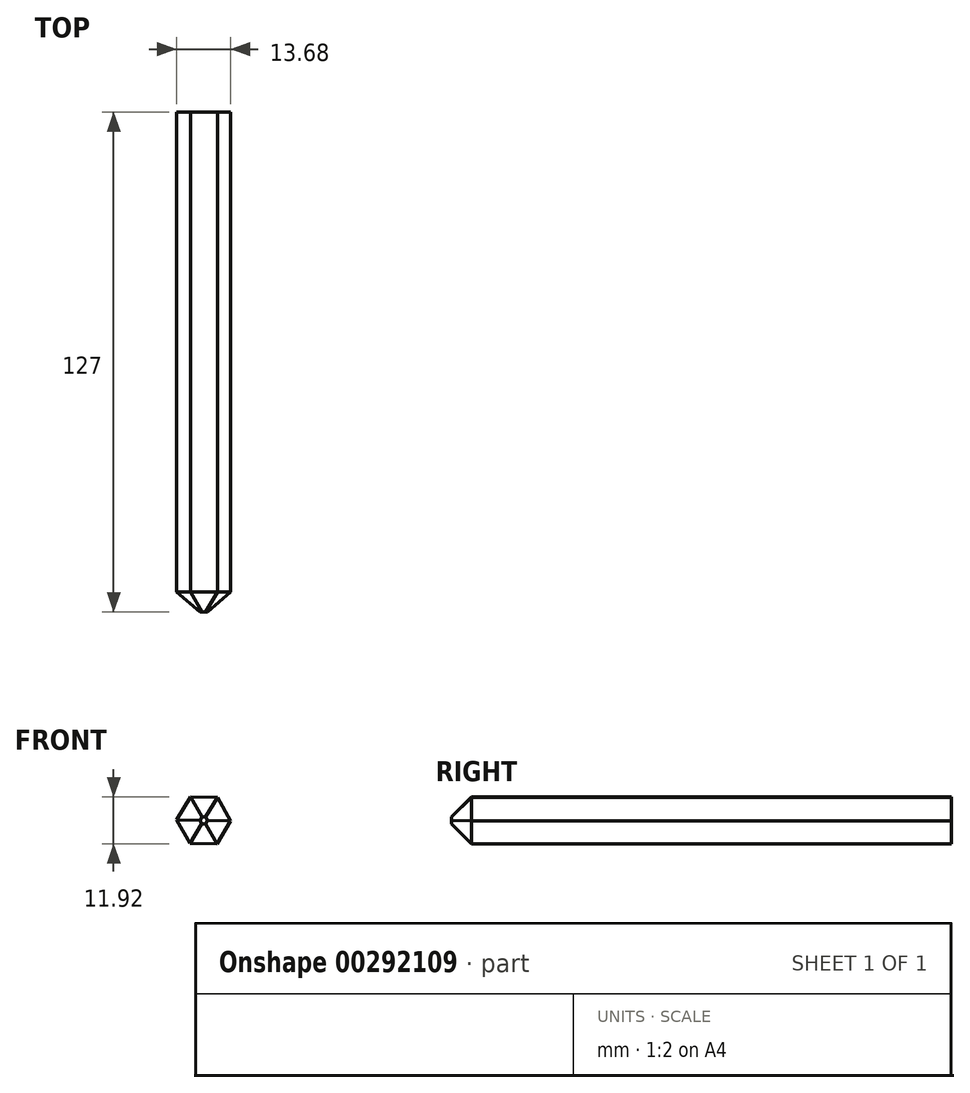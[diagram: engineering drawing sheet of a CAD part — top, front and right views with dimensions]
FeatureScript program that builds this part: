
annotation { "Feature Type Name" : "Feature", "Feature Type Description" : "" }
export const myFeature = defineFeature(function(context is Context, id is Id, definition is map)
    precondition{}
    {
        {
            var Q0;
            Q0=qCreatedBy(makeId("Front.planeOp"),FACE);
            var sketch = newSketch(context, id + "F0", { "sketchPlane" : qUnion([Q0])});
            skCircle(sketch, "E0", {"center": v(0, 0) * mm, "radius": 6.97 * mm});
            skSolve(sketch);
        }
        {
            var Q0;
            Q0=qCreatedBy(makeId("Front.planeOp"),FACE);
            var sketch = newSketch(context, id + "F1", { "sketchPlane" : qUnion([Q0])});
            skCircle(sketch, "E1.cCircle", {"center": v(0, 0) * mm, "radius": 5.92 * mm, "construction": true});
            skLineSegment(sketch, "E1.0", {"start": v(3.49, 5.88) * mm, "end": v(6.84, -0.08) * mm});
            skLineSegment(sketch, "E1.1", {"start": v(6.84, -0.08) * mm, "end": v(3.35, -5.96) * mm});
            skLineSegment(sketch, "E1.2", {"start": v(3.35, -5.96) * mm, "end": v(-3.49, -5.88) * mm});
            skLineSegment(sketch, "E1.3", {"start": v(-3.49, -5.88) * mm, "end": v(-6.84, 0.08) * mm});
            skLineSegment(sketch, "E1.4", {"start": v(-6.84, 0.08) * mm, "end": v(-3.35, 5.96) * mm});
            skLineSegment(sketch, "E1.5", {"start": v(-3.35, 5.96) * mm, "end": v(3.49, 5.88) * mm});
            skPoint(sketch, "E1.0.midPoint", {"position": v(5.16, 2.9) * mm});
            skSolve(sketch);
        }
        {
            var Q0;
            Q0=makeQuery(id+"F1.imprint","IMPRINT",FACE,{"disambiguationData":[TD([[makeQuery(id+"F1.imprint","IMPRINT",EDGE,{"derivedFrom":sQuery(id+"F1.wireOp",EDGE,"E1.0")}),-1.0]])]});
            extrude(context, id + "F2", {"entities" : qUnion([Q0]), "depth" : 127 * mm});
        }
        {
            var Q0;
            Q0=sQuery(id+"F0.wireOp",EDGE,"E0");
            extrude(context, id + "F3", {"bodyType" : ToolBodyType.SURFACE, "surfaceEntities" : qUnion([Q0]), "depth" : 20 * mm});
        }
        {
            var Q0;
            Q0=makeQuery(id+"F2.opExtrude","CAP_EDGE",EDGE,{"disambiguationData":[OSD([sQuery(id+"F1.wireOp",EDGE,"E1.0")])],"isStart":false});
            var Q1;
            Q1=makeQuery(id+"F2.opExtrude","CAP_FACE",FACE,{"disambiguationData":[OSD([sQuery(id+"F1.wireOp",EDGE,"E1.0"),sQuery(id+"F1.wireOp",EDGE,"E1.1"),sQuery(id+"F1.wireOp",EDGE,"E1.2"),sQuery(id+"F1.wireOp",EDGE,"E1.3"),sQuery(id+"F1.wireOp",EDGE,"E1.4"),sQuery(id+"F1.wireOp",EDGE,"E1.5")])],"isStart":false});
            chamfer(context, id + "F4", {"entities" : qUnion([Q0, Q1]), "width" : 5.08 * mm, "tangentPropagation" : true});
        }
    });
